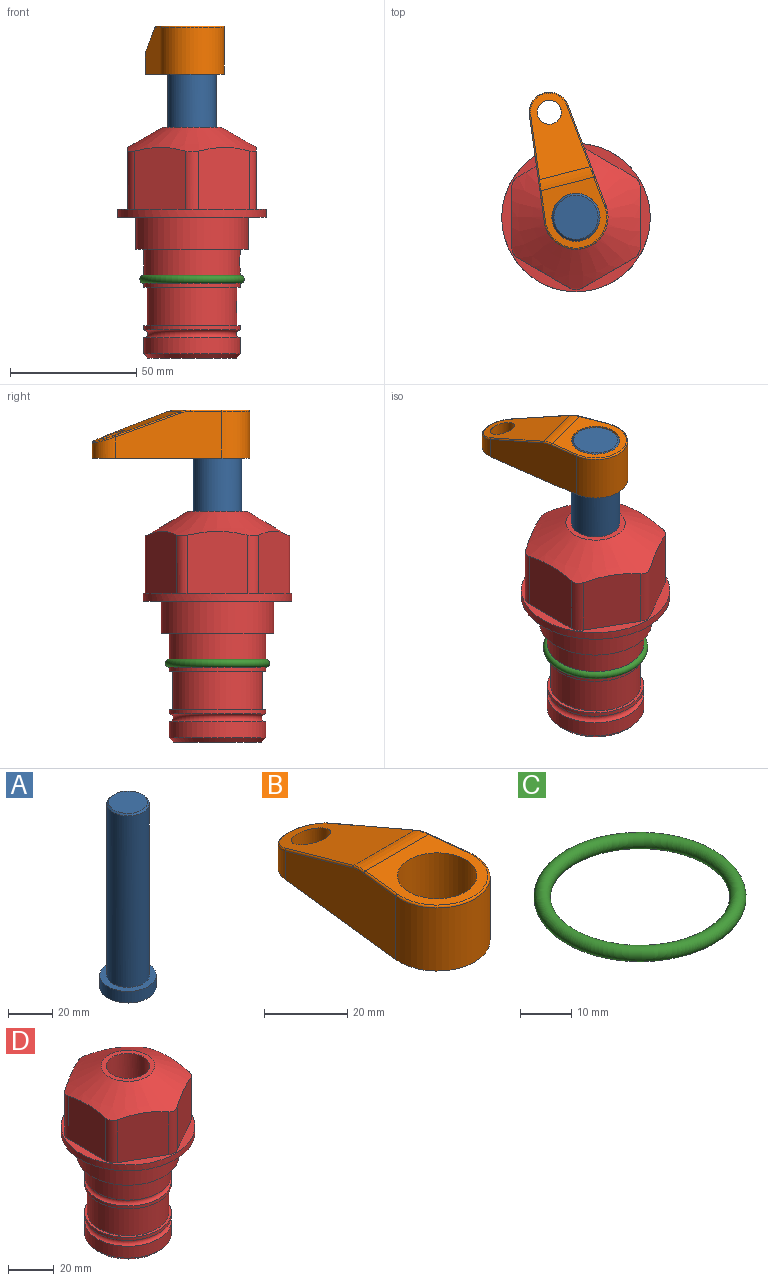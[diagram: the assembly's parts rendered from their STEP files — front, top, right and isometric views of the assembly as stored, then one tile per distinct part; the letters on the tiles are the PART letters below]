
ASSEMBLY  parts=4 mates=2
PART A: 6 faces, bbox 25.4x25.4x101.6 mm
  f0: plane 17.46x17.46mm, normal (0,0,1), area 239.5mm2, adj f5
  f1: plane 25.4x25.4mm, normal (0,0,-1), area 506.7mm2, adj f2
  f2: cylinder r=12.7mm len=25.4mm, axis (0,0,1), area 506.7mm2, adj f1,f3
  f3: plane 25.4x25.4mm, normal (0,0,1), area 221.7mm2, adj f2,f4
  f4: cylinder r=9.53mm len=94.46mm, axis (0,0,1), area 5653mm2, adj f3,f5
  f5: cone r=8.73mm half-angle=45deg, axis (0,0,-1), area 64.4mm2, adj f0,f4
PART B: 44 faces, bbox 27.5x64.5x19.1 mm
  f0: plane 2.3x0.95mm, normal (0,0,-1), area 1mm2, adj f25,f30,f34
  f1: plane 63.5x25.4mm, normal (0,0,-1), area 561.7mm2, adj f2,f3,f4,f5,f6,f7,f19,f20
  f2: cylinder r=12.7mm len=25.4mm, axis (0,0,-1), area 792.2mm2, adj f1,f3,f5,f13
  f3: plane 42.33x18.54mm, normal (0.99,0.11,0), area 647mm2, adj f1,f2,f4,f11,f12,f14
  f4: cylinder r=7.94mm len=15.78mm, axis (0,0,-1), area 158.6mm2, adj f1,f3,f5,f16
  f5: plane 42.33x18.54mm, normal (-0.99,0.11,0), area 647mm2, adj f1,f2,f4,f15,f17,f18
  f6: cylinder r=9.53mm len=19.05mm, axis (0,0,-1), area 1140.1mm2, adj f1,f8
  f7: cylinder r=4.76mm len=10.98mm, axis (0,0,-1), area 276.1mm2, adj f1,f9
  f8: plane 25.83x24.38mm, normal (0,0,1), area 262.2mm2, adj f6,f10,f11,f13,f15
  f9: plane 32.49x20.55mm, normal (0,0.34,0.94), area 489.9mm2, adj f7,f10,f14,f16,f18
  f10: cylinder r=12.7mm len=21.49mm, axis (-1,0,0), area 93.2mm2, adj f8,f9,f12,f17
  f11: cylinder r=0.51mm len=12.34mm, axis (0.11,-0.99,0), area 9.9mm2, adj f3,f8,f12,f13
  f12: bspline ~7.62x1.64mm, area 3.5mm2, adj f3,f10,f11,f14
  f13: torus R=12.19mm, axis (0,0,1), area 33.6mm2, adj f2,f8,f11,f15
  f14: cylinder r=0.51mm len=26.01mm, axis (0.1,-0.93,0.34), area 21.6mm2, adj f3,f9,f12,f16
  f15: cylinder r=0.51mm len=12.34mm, axis (0.11,0.99,0), area 9.9mm2, adj f5,f8,f13,f17
  f16: bspline ~15.78x7.05mm, area 15.7mm2, adj f4,f9,f14,f18
  f17: bspline ~7.62x1.64mm, area 3.5mm2, adj f5,f10,f15,f18
  f18: cylinder r=0.51mm len=26.01mm, axis (0.1,0.93,-0.34), area 21.6mm2, adj f5,f9,f16,f17
  f19: plane 21.6x14.29mm, normal (-0.99,-0.11,0), area 242.6mm2, adj f1,f26,f28,f34,f36,f38
  f20: plane 21.6x14.29mm, normal (0.99,-0.11,0), area 242.6mm2, adj f1,f27,f29,f37,f39,f41
  f21: cylinder r=12.7mm len=14.29mm, axis (0,0,-1), area 173.2mm2, adj f1,f26,f27,f30,f31,f33
  f22: cylinder r=7.94mm len=7.63mm, axis (0,0,-1), area 53.8mm2, adj f1,f28,f29,f42
  f23: plane 2.3x0.95mm, normal (0,0,-1), area 1mm2, adj f25,f33,f37
  f24: plane 17.94x12.32mm, normal (0,-0.34,-0.94), area 191.2mm2, adj f25,f38,f41,f42
  f25: cylinder r=9.53mm len=12.93mm, axis (-1,0,0), area 37.5mm2, adj f0,f23,f24,f31,f36,f39
  f26: cylinder r=1.59mm len=14.29mm, axis (0,0,-1), area 49mm2, adj f1,f19,f21,f32
  f27: cylinder r=1.59mm len=14.29mm, axis (0,0,-1), area 49mm2, adj f1,f20,f21,f35
  f28: cylinder r=1.59mm len=7.28mm, axis (0,0,-1), area 22.1mm2, adj f1,f19,f22,f40
  f29: cylinder r=1.59mm len=7.28mm, axis (0,0,-1), area 22.1mm2, adj f1,f20,f22,f43
  f30: torus R=14.29mm, axis (0,0,1), area 5.8mm2, adj f0,f21,f31,f32
  f31: bspline ~11.06x2.73mm, area 20.8mm2, adj f21,f25,f30,f33
  f32: sphere r=1.59mm, area 5.4mm2, adj f26,f30,f34
  f33: torus R=14.29mm, axis (0,0,1), area 5.8mm2, adj f21,f23,f31,f35
  f34: cylinder r=1.59mm len=1.68mm, axis (-0.11,0.99,0), area 2.4mm2, adj f0,f19,f32,f36
  f35: sphere r=1.59mm, area 5.4mm2, adj f27,f33,f37
  f36: bspline ~5.82x2.33mm, area 7.7mm2, adj f19,f25,f34,f38
  f37: cylinder r=1.59mm len=1.68mm, axis (0.11,0.99,0), area 2.4mm2, adj f20,f23,f35,f39
  f38: cylinder r=1.59mm len=18.33mm, axis (0.1,-0.93,0.34), area 46.7mm2, adj f19,f24,f36,f40
  f39: bspline ~5.82x2.33mm, area 7.7mm2, adj f20,f25,f37,f41
  f40: sphere r=1.59mm, area 3.6mm2, adj f28,f38,f42
  f41: cylinder r=1.59mm len=18.33mm, axis (0.1,0.93,-0.34), area 46.7mm2, adj f20,f24,f39,f43
  f42: bspline ~8.31x1.84mm, area 15.3mm2, adj f22,f24,f40,f43
  f43: sphere r=1.59mm, area 3.6mm2, adj f29,f41,f42
PART C: 1 faces, bbox 44.7x44.7x3.2 mm
  f0: torus R=19.05mm, axis (0,0,1), area 1193.9mm2
PART D: 36 faces, bbox 58.7x58.7x91.2 mm
  f0: cylinder r=17.78mm len=35.56mm, axis (0,0,1), area 1670.8mm2, adj f23,f24,f31
  f1: cylinder r=19.05mm len=38.1mm, axis (0,0,1), area 1191.9mm2, adj f26,f27,f30
  f2: plane 58.66x58.66mm, normal (0,0,-1), area 1150.6mm2, adj f3,f28
  f3: cylinder r=29.33mm len=58.66mm, axis (0,0,-1), area 585.1mm2, adj f2,f4
  f4: plane 58.66x58.66mm, normal (0,0,1), area 475.9mm2, adj f3,f5,f6,f7,f8,f9,f10,f11
  f5: plane 24.5x20.32mm, normal (-0.5,0.87,0), area 562.8mm2, adj f4,f15,f16,f17
  f6: plane 24.5x20.32mm, normal (0.5,0.87,0), area 562.8mm2, adj f4,f14,f15,f17
  f7: plane 24.5x23.48mm, normal (1,0,0), area 562.8mm2, adj f4,f13,f14,f17
  f8: plane 24.5x20.32mm, normal (0.5,-0.87,0), area 562.8mm2, adj f4,f12,f13,f17
  f9: plane 24.5x20.32mm, normal (-0.5,-0.87,0), area 562.8mm2, adj f4,f11,f12,f17
  f10: plane 24.5x23.48mm, normal (-1,0,0), area 562.8mm2, adj f4,f11,f16,f17
  f11: cylinder r=5.08mm len=23.01mm, axis (0,0,-1), area 121.2mm2, adj f4,f9,f10,f17
  f12: cylinder r=5.08mm len=23.01mm, axis (0,0,-1), area 121.2mm2, adj f4,f8,f9,f17
  f13: cylinder r=5.08mm len=23.01mm, axis (0,0,-1), area 121.2mm2, adj f4,f7,f8,f17
  f14: cylinder r=5.08mm len=23.01mm, axis (0,0,-1), area 121.2mm2, adj f4,f6,f7,f17
  f15: cylinder r=5.08mm len=23.01mm, axis (0,0,-1), area 121.2mm2, adj f4,f5,f6,f17
  f16: cylinder r=5.08mm len=23.01mm, axis (0,0,-1), area 121.2mm2, adj f4,f5,f10,f17
  f17: cone r=11.73mm half-angle=60deg, axis (0,0,-1), area 2071.8mm2, adj f5,f6,f7,f8,f9,f10,f11,f12
  f18: plane 23.46x23.46mm, normal (0,0,1), area 147.4mm2, adj f17,f35
  f19: plane 34.93x34.93mm, normal (0,0,-1), area 958mm2, adj f29
  f20: cylinder r=19.05mm len=38.1mm, axis (0,0,1), area 760.1mm2, adj f21,f29
  f21: torus R=19.05mm, axis (0,0,1), area 565.3mm2, adj f20,f22
  f22: cylinder r=19.05mm len=38.1mm, axis (0,0,1), area 190mm2, adj f21,f23
  f23: plane 38.1x38.1mm, normal (0,0,1), area 146.9mm2, adj f0,f22
  f24: plane 38.1x38.1mm, normal (0,0,-1), area 146.9mm2, adj f0,f25
  f25: cylinder r=19.05mm len=38.1mm, axis (0,0,1), area 190mm2, adj f24,f26
  f26: torus R=19.05mm, axis (0,0,1), area 565.3mm2, adj f1,f25
  f27: plane 44.45x44.45mm, normal (0,0,-1), area 411.7mm2, adj f1,f28
  f28: cylinder r=22.23mm len=44.45mm, axis (0,0,1), area 1773.5mm2, adj f2,f27
  f29: cone r=19.05mm half-angle=45deg, axis (0,0,1), area 257.5mm2, adj f19,f20
  f30: cylinder r=3.17mm len=6.75mm, axis (-1,0,0), area 128mm2, adj f1,f33
  f31: cylinder r=3.17mm len=6.35mm, axis (-1,0,0), area 102.5mm2, adj f0,f33
  f32: plane 25.4x25.4mm, normal (0,0,1), area 506.7mm2, adj f33
  f33: cylinder r=12.7mm len=66.42mm, axis (0,0,-1), area 5236.2mm2, adj f30,f31,f32,f34
  f34: cone r=9.53mm half-angle=30deg, axis (0,0,-1), area 443.4mm2, adj f33,f35
  f35: cylinder r=9.53mm len=19.05mm, axis (0,0,-1), area 849mm2, adj f18,f34
PLACE A rot(axis=(0,0,1),104.2deg) t=(0,0,2.03)mm
PLACE B rot(axis=(0,0,1),14.2deg) t=(0,0,56.64)mm
PLACE C at identity
PLACE D at identity fixed
MATE cylindrical A.f2 <-> D.f0  axis (0,0,1) through (0,0,27.67)mm
MATE fastened B.f2 <-> A.f2  axis (0,0,-1) through (0,0,75.69)mm
